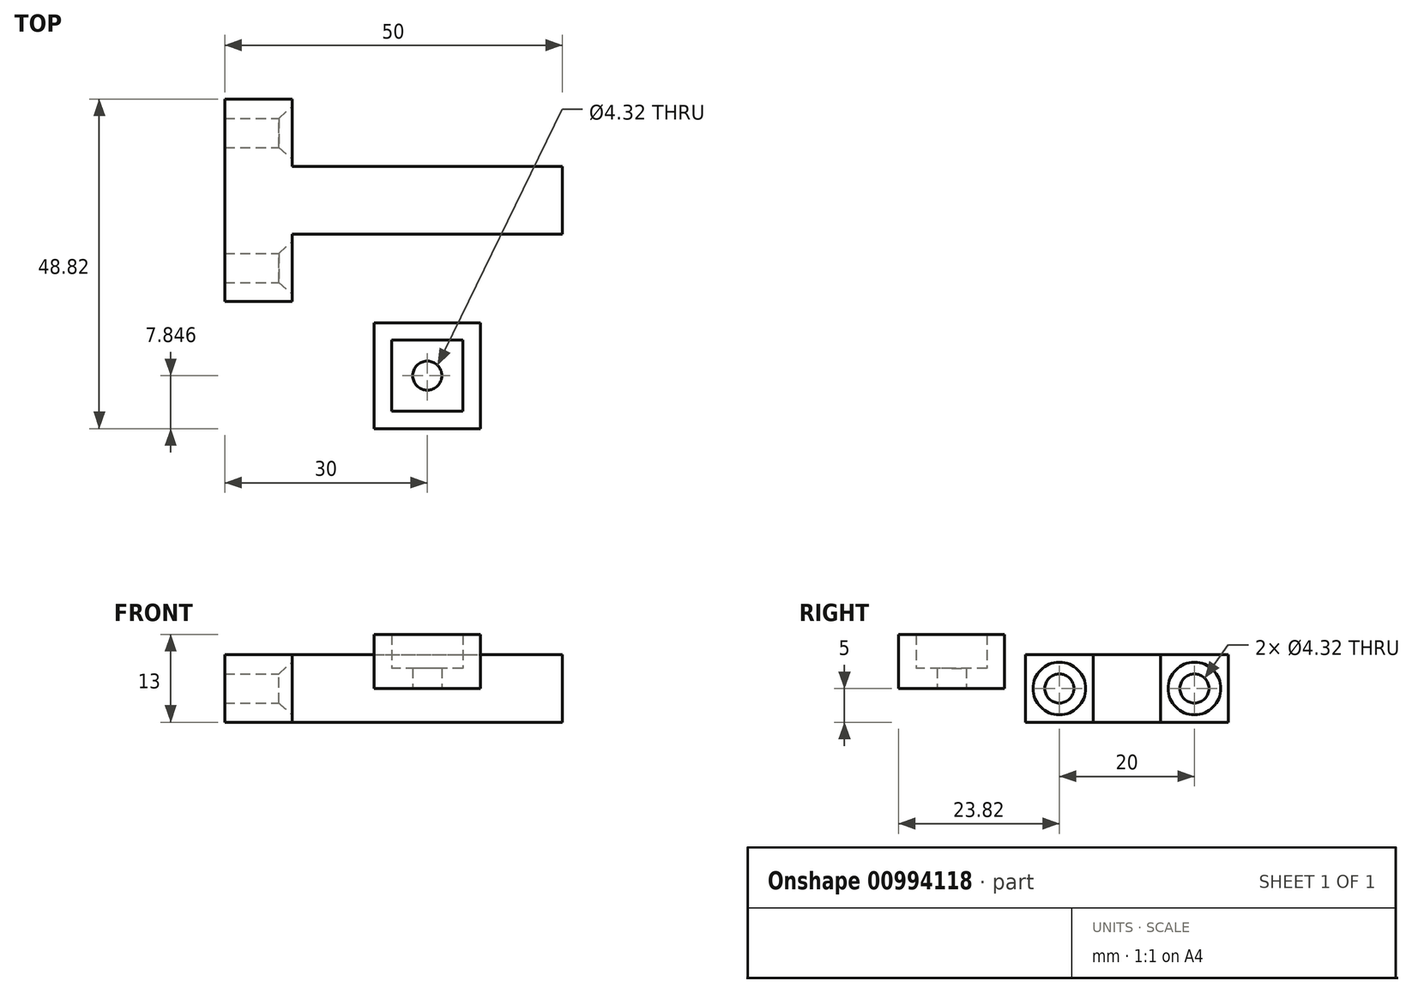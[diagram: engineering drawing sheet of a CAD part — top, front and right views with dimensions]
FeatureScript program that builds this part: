
annotation { "Feature Type Name" : "Feature", "Feature Type Description" : "" }
export const myFeature = defineFeature(function(context is Context, id is Id, definition is map)
    precondition{}
    {
        {
            var Q0;
            Q0=qCreatedBy(makeId("Top.planeOp"),FACE);
            var sketch = newSketch(context, id + "F0", { "sketchPlane" : qUnion([Q0])});
            skLineSegment(sketch, "E0.bottom", {"start": v(-20, 5) * mm, "end": v(20, 5) * mm});
            skLineSegment(sketch, "E0.top", {"start": v(-20, -5) * mm, "end": v(20, -5) * mm});
            skLineSegment(sketch, "E0.right", {"start": v(20, 5) * mm, "end": v(20, -5) * mm});
            skPoint(sketch, "E0.middle", {"position": v(0, 0) * mm});
            skLineSegment(sketch, "E1.bottom", {"start": v(-20, -15) * mm, "end": v(-30, -15) * mm});
            skLineSegment(sketch, "E1.top", {"start": v(-20, 15) * mm, "end": v(-30, 15) * mm});
            skLineSegment(sketch, "E1.left", {"start": v(-20, -15) * mm, "end": v(-20, 15) * mm});
            skLineSegment(sketch, "E1.right", {"start": v(-30, -15) * mm, "end": v(-30, 15) * mm});
            skPoint(sketch, "E1.middle", {"position": v(-25, 0) * mm});
            skSolve(sketch);
        }
        {
            var Q0;
            Q0 = qSketchRegion(id + "F0", true);
            extrude(context, id + "F1", {"entities" : qUnion([Q0]), "endBound" : BoundingType.SYMMETRIC, "depth" : 10 * mm, "offsetDistance" : 25 * mm});
        }
        {
            var Q0;
            {var subQ0=sQuery(id+"F0.wireOp",EDGE,"E1.left");Q0=makeQuery(id+"F1.opExtrude","SWEPT_FACE",FACE,{"disambiguationData":[OSD([subQ0]),TDD([makeQuery(id+"F0.imprint","IMPRINT",EDGE,{"disambiguationData":[TD([[makeQuery(id+"F0.imprint","INTERSECT",VERTEX,{"derivedFrom":[sQuery(id+"F0.wireOp",EDGE,"E0.bottom"),subQ0]}),-1.0]])],"derivedFrom":subQ0})])]});}
            var sketch = newSketch(context, id + "F2", { "sketchPlane" : qUnion([Q0])});
            skLineSegment(sketch, "E2", {"start": v(15, 5) * mm, "end": v(5, -5) * mm});
            skLineSegment(sketch, "E3", {"start": v(5, 5) * mm, "end": v(15, -5) * mm});
            skPoint(sketch, "E4", {"position": v(10, 0) * mm});
            skSolve(sketch);
        }
        {
            var Q0;
            Q0=sQuery(id+"F2.wireOp",VERTEX,"E4");
            var Q1;
            Q1=makeQuery(id+"F1.opExtrude","SWEPT_BODY",BODY,{"disambiguationData":[OSD([sQuery(id+"F0.wireOp",EDGE,"E0.bottom"),sQuery(id+"F0.wireOp",EDGE,"E0.top"),sQuery(id+"F0.wireOp",EDGE,"E0.right"),sQuery(id+"F0.wireOp",EDGE,"E1.bottom"),sQuery(id+"F0.wireOp",EDGE,"E1.top"),sQuery(id+"F0.wireOp",EDGE,"E1.left"),sQuery(id+"F0.wireOp",EDGE,"E1.right")])]});
            hole(context, id + "F3", {"style" : HoleStyle.C_SINK, "endStyle" : HoleEndStyle.BLIND, "standardTappedOrClearance" : lookupTablePath({ "fit" : "Normal (ASME)", "standard" : "ANSI", "size" : "#6", "type" : "Clearance" }), "standardBlindInLast" : lookupTablePath({ "fit" : "Normal", "standard" : "ANSI", "engagement" : "75%", "pitch" : "32 tpi", "size" : "#6", "type" : "Clearance & tapped" }), "holeDiameter" : 4.32 * mm, "cSinkDiameter" : 7.8 * mm, "cSinkAngle" : 82 * degree, "majorDiameter" : 5 * mm, "holeDepth" : 10 * mm, "isTappedThrough" : true, "tappedDepth" : 2.5 * mm, "tapClearance" : 3, "startFromSketch" : true, "locations" : qUnion([Q0]), "scope" : qUnion([Q1])});
        }
        {
            var Q0;
            {var subQ0=sQuery(id+"F0.wireOp",EDGE,"E1.left");Q0=makeQuery(id+"F1.opExtrude","SWEPT_FACE",FACE,{"disambiguationData":[OSD([subQ0]),TDD([makeQuery(id+"F0.imprint","IMPRINT",EDGE,{"disambiguationData":[TD([[makeQuery(id+"F0.imprint","INTERSECT",VERTEX,{"derivedFrom":[sQuery(id+"F0.wireOp",EDGE,"E0.top"),subQ0]}),1.0]])],"derivedFrom":subQ0})])]});}
            var sketch = newSketch(context, id + "F4", { "sketchPlane" : qUnion([Q0])});
            skLineSegment(sketch, "E5", {"start": v(-15, -5) * mm, "end": v(-5, -5) * mm});
            skPoint(sketch, "E6", {"position": v(-10, 0) * mm});
            skSolve(sketch);
        }
        {
            var Q0;
            Q0=sQuery(id+"F4.wireOp",VERTEX,"E6");
            var Q1;
            Q1=makeQuery(id+"F1.opExtrude","SWEPT_BODY",BODY,{"disambiguationData":[OSD([sQuery(id+"F0.wireOp",EDGE,"E0.bottom"),sQuery(id+"F0.wireOp",EDGE,"E0.top"),sQuery(id+"F0.wireOp",EDGE,"E0.right"),sQuery(id+"F0.wireOp",EDGE,"E1.bottom"),sQuery(id+"F0.wireOp",EDGE,"E1.top"),sQuery(id+"F0.wireOp",EDGE,"E1.left"),sQuery(id+"F0.wireOp",EDGE,"E1.right")])]});
            hole(context, id + "F5", {"style" : HoleStyle.C_SINK, "endStyle" : HoleEndStyle.BLIND, "standardTappedOrClearance" : lookupTablePath({ "fit" : "Normal (ASME)", "standard" : "ANSI", "size" : "#6", "type" : "Clearance" }), "standardBlindInLast" : lookupTablePath({ "fit" : "Normal", "standard" : "ANSI", "engagement" : "75%", "pitch" : "32 tpi", "size" : "#6", "type" : "Clearance & tapped" }), "holeDiameter" : 4.32 * mm, "cSinkDiameter" : 7.8 * mm, "cSinkAngle" : 82 * degree, "majorDiameter" : 5 * mm, "holeDepth" : 10 * mm, "isTappedThrough" : true, "tappedDepth" : 2.5 * mm, "tapClearance" : 3, "startFromSketch" : true, "locations" : qUnion([Q0]), "scope" : qUnion([Q1])});
        }
        {
            var Q0;
            Q0=qCreatedBy(makeId("Top.planeOp"),FACE);
            var sketch = newSketch(context, id + "F6", { "sketchPlane" : qUnion([Q0])});
            skLineSegment(sketch, "E7.bottom", {"start": v(5.25, -20.72) * mm, "end": v(-5.25, -20.72) * mm});
            skLineSegment(sketch, "E7.top", {"start": v(5.25, -31.22) * mm, "end": v(-5.25, -31.22) * mm});
            skLineSegment(sketch, "E7.left", {"start": v(5.25, -20.72) * mm, "end": v(5.25, -31.22) * mm});
            skLineSegment(sketch, "E7.right", {"start": v(-5.25, -20.72) * mm, "end": v(-5.25, -31.22) * mm});
            skPoint(sketch, "E7.middle", {"position": v(0, -25.97) * mm});
            skLineSegment(sketch, "E8.0", {"start": v(7.85, -33.82) * mm, "end": v(-7.85, -33.82) * mm});
            skLineSegment(sketch, "E8.1", {"start": v(7.85, -18.12) * mm, "end": v(7.85, -33.82) * mm});
            skLineSegment(sketch, "E8.2", {"start": v(7.85, -18.12) * mm, "end": v(-7.85, -18.12) * mm});
            skLineSegment(sketch, "E8.3", {"start": v(-7.85, -18.12) * mm, "end": v(-7.85, -33.82) * mm});
            skSolve(sketch);
        }
        {
            var Q0;
            Q0=makeQuery(id+"F6.imprint","IMPRINT",FACE,{"disambiguationData":[TD([[makeQuery(id+"F6.imprint","IMPRINT",EDGE,{"derivedFrom":sQuery(id+"F6.wireOp",EDGE,"E7.bottom")}),1.0]])]});
            extrude(context, id + "F7", {"entities" : qUnion([Q0]), "depth" : 3 * mm, "offsetDistance" : 25 * mm});
        }
        {
            var Q0;
            Q0=sQuery(id+"F6.wireOp",VERTEX,"E7.middle");
            var Q1;
            Q1=makeQuery(id+"F7.opExtrude","SWEPT_BODY",BODY,{"disambiguationData":[OSD([sQuery(id+"F6.wireOp",EDGE,"E7.bottom"),sQuery(id+"F6.wireOp",EDGE,"E7.top"),sQuery(id+"F6.wireOp",EDGE,"E7.left"),sQuery(id+"F6.wireOp",EDGE,"E7.right")])]});
            hole(context, id + "F8", {"style" : HoleStyle.SIMPLE, "endStyle" : HoleEndStyle.BLIND, "oppositeDirection" : true, "standardTappedOrClearance" : lookupTablePath({ "fit" : "Normal (ASME)", "standard" : "ANSI", "size" : "#6", "type" : "Clearance" }), "standardBlindInLast" : lookupTablePath({ "fit" : "Normal", "standard" : "ANSI", "engagement" : "75%", "pitch" : "32 tpi", "size" : "#6", "type" : "Clearance & tapped" }), "holeDiameter" : 4.32 * mm, "majorDiameter" : 5 * mm, "holeDepth" : 4 * mm, "isTappedThrough" : true, "tappedDepth" : 2.5 * mm, "tapClearance" : 3, "startFromSketch" : true, "locations" : qUnion([Q0]), "scope" : qUnion([Q1])});
        }
        {
            var Q0;
            Q0=makeQuery(id+"F6.imprint","IMPRINT",FACE,{"disambiguationData":[TD([[makeQuery(id+"F6.imprint","IMPRINT",EDGE,{"derivedFrom":sQuery(id+"F6.wireOp",EDGE,"E7.bottom")}),-1.0]])]});
            extrude(context, id + "F9", {"entities" : qUnion([Q0]), "operationType" : NewBodyOperationType.ADD, "depth" : 8 * mm, "offsetDistance" : 25 * mm});
        }
    });
